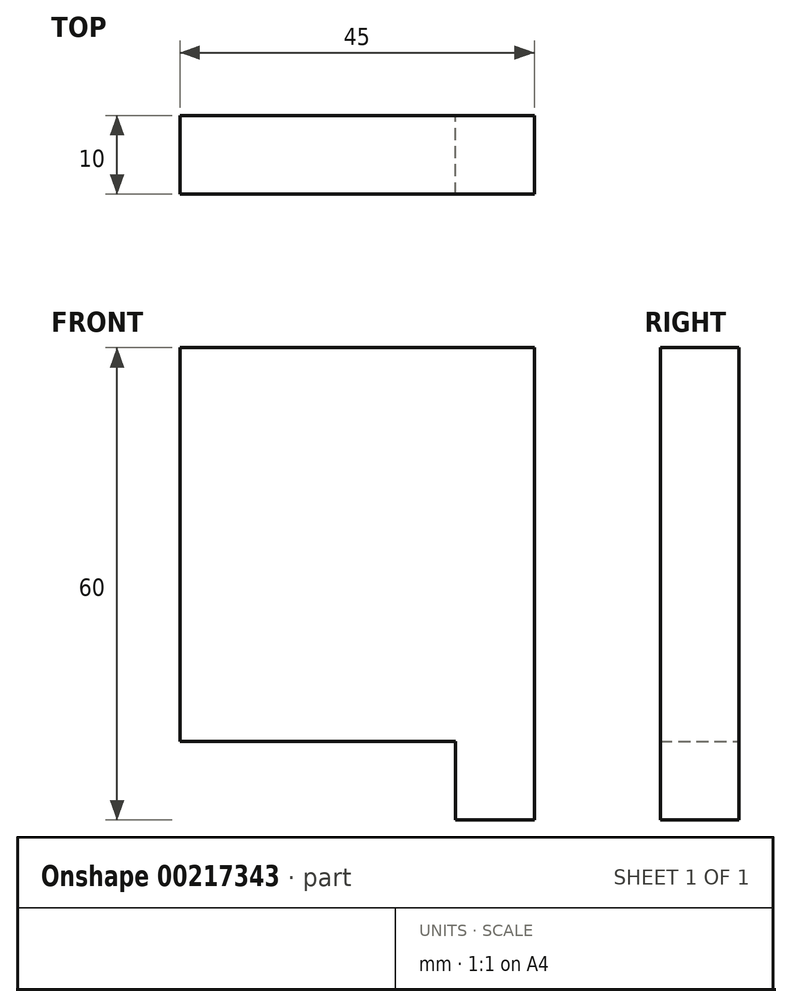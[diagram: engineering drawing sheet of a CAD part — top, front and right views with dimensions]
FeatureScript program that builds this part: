
annotation { "Feature Type Name" : "Feature", "Feature Type Description" : "" }
export const myFeature = defineFeature(function(context is Context, id is Id, definition is map)
    precondition{}
    {
        {
            var Q0;
            Q0=qCreatedBy(makeId("Front.planeOp"),FACE);
            var sketch = newSketch(context, id + "F0", { "sketchPlane" : qUnion([Q0])});
            skLineSegment(sketch, "E0.bottom", {"start": v(22.5, 25) * mm, "end": v(-22.5, 25) * mm});
            skLineSegment(sketch, "E0.top", {"start": v(22.5, -25) * mm, "end": v(-22.5, -25) * mm});
            skLineSegment(sketch, "E0.left", {"start": v(22.5, 25) * mm, "end": v(22.5, -25) * mm});
            skLineSegment(sketch, "E0.right", {"start": v(-22.5, 25) * mm, "end": v(-22.5, -25) * mm});
            skPoint(sketch, "E0.middle", {"position": v(0, 0) * mm});
            skSolve(sketch);
        }
        {
            var Q0;
            Q0=makeQuery(id+"F0.imprint","IMPRINT",FACE,{"disambiguationData":[TD([[makeQuery(id+"F0.imprint","IMPRINT",EDGE,{"derivedFrom":sQuery(id+"F0.wireOp",EDGE,"E0.bottom")}),1.0]])]});
            extrude(context, id + "F1", {"entities" : qUnion([Q0]), "depth" : 10 * mm});
        }
        {
            var Q0;
            Q0=makeQuery(id+"F1.opExtrude","SWEPT_FACE",FACE,{"disambiguationData":[OSD([sQuery(id+"F0.wireOp",EDGE,"E0.top")])]});
            var sketch = newSketch(context, id + "F2", { "sketchPlane" : qUnion([Q0])});
            skLineSegment(sketch, "E1.bottom", {"start": v(22.5, 10) * mm, "end": v(12.5, 10) * mm});
            skLineSegment(sketch, "E1.top", {"start": v(22.5, 0) * mm, "end": v(12.5, 0) * mm});
            skLineSegment(sketch, "E1.left", {"start": v(22.5, 10) * mm, "end": v(22.5, 0) * mm});
            skLineSegment(sketch, "E1.right", {"start": v(12.5, 10) * mm, "end": v(12.5, 0) * mm});
            skSolve(sketch);
        }
        {
            var Q0;
            Q0=makeQuery(id+"F2.imprint","IMPRINT",FACE,{"disambiguationData":[TD([[makeQuery(id+"F2.imprint","IMPRINT",EDGE,{"derivedFrom":sQuery(id+"F2.wireOp",EDGE,"E1.bottom")}),1.0]])]});
            extrude(context, id + "F3", {"entities" : qUnion([Q0]), "operationType" : NewBodyOperationType.ADD, "depth" : 10 * mm});
        }
    });
